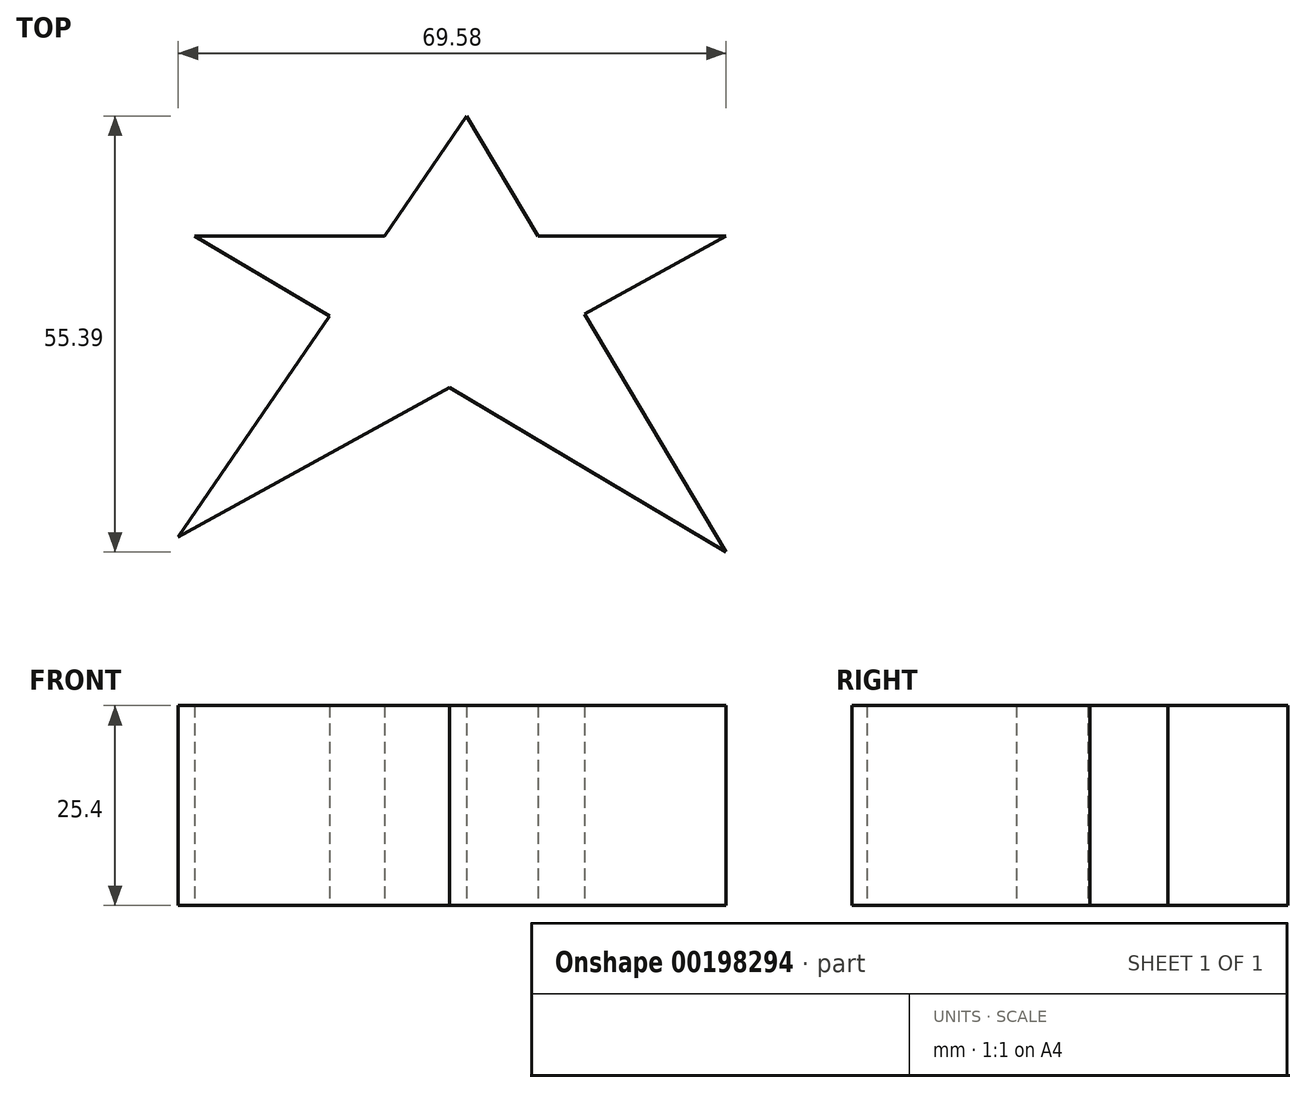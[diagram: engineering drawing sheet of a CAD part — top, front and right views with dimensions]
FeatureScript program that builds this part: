
annotation { "Feature Type Name" : "Feature", "Feature Type Description" : "" }
export const myFeature = defineFeature(function(context is Context, id is Id, definition is map)
    precondition{}
    {
        {
            var Q0;
            Q0=qCreatedBy(makeId("Top.planeOp"),FACE);
            var sketch = newSketch(context, id + "F0", { "sketchPlane" : qUnion([Q0])});
            skLineSegment(sketch, "E0", {"start": v(-42.06, -14.1) * mm, "end": v(-5.43, 39.35) * mm});
            skLineSegment(sketch, "E1", {"start": v(-5.43, 39.35) * mm, "end": v(27.52, -16.04) * mm});
            skLineSegment(sketch, "E2", {"start": v(27.52, -16.04) * mm, "end": v(-39.96, 24.1) * mm});
            skLineSegment(sketch, "E3", {"start": v(-39.96, 24.1) * mm, "end": v(27.52, 24.1) * mm});
            skLineSegment(sketch, "E4", {"start": v(27.52, 24.1) * mm, "end": v(-42.06, -14.1) * mm});
            skSolve(sketch);
        }
        {
            var Q0;
            {var subQ1=sQuery(id+"F0.wireOp",EDGE,"E0");var subQ5=sQuery(id+"F0.wireOp",EDGE,"E2");var subQ6=makeQuery(id+"F0.imprint","INTERSECT",VERTEX,{"derivedFrom":[subQ1,subQ5]});Q0=makeQuery(id+"F0.imprint","IMPRINT",FACE,{"disambiguationData":[TD([[makeQuery(id+"F0.imprint","IMPRINT",EDGE,{"disambiguationData":[TD([[subQ6,-1.0]])],"derivedFrom":subQ1}),-1.0]])]});}
            var Q1;
            {var subQ0=sQuery(id+"F0.wireOp",EDGE,"E2");var subQ1=sQuery(id+"F0.wireOp",EDGE,"E0");var subQ2=makeQuery(id+"F0.imprint","INTERSECT",VERTEX,{"derivedFrom":[subQ1,subQ0]});Q1=makeQuery(id+"F0.imprint","IMPRINT",FACE,{"disambiguationData":[TD([[makeQuery(id+"F0.imprint","IMPRINT",EDGE,{"disambiguationData":[TD([[subQ2,-1.0]])],"derivedFrom":subQ1}),1.0]])]});}
            var Q2;
            {var subQ0=sQuery(id+"F0.wireOp",EDGE,"E3");var subQ1=sQuery(id+"F0.wireOp",EDGE,"E1");var subQ2=makeQuery(id+"F0.imprint","INTERSECT",VERTEX,{"derivedFrom":[subQ1,subQ0]});Q2=makeQuery(id+"F0.imprint","IMPRINT",FACE,{"disambiguationData":[TD([[makeQuery(id+"F0.imprint","IMPRINT",EDGE,{"disambiguationData":[TD([[subQ2,-1.0]])],"derivedFrom":subQ1}),1.0]])]});}
            var Q3;
            {var subQ0=sQuery(id+"F0.wireOp",EDGE,"E1");var subQ1=sQuery(id+"F0.wireOp",EDGE,"E0");var subQ2=makeQuery(id+"F0.imprint","INTERSECT",VERTEX,{"derivedFrom":[subQ1,subQ0]});Q3=makeQuery(id+"F0.imprint","IMPRINT",FACE,{"disambiguationData":[TD([[makeQuery(id+"F0.imprint","IMPRINT",EDGE,{"disambiguationData":[TD([[subQ2,1.0]])],"derivedFrom":subQ1}),-1.0]])]});}
            var Q4;
            {var subQ0=sQuery(id+"F0.wireOp",EDGE,"E4");var subQ1=sQuery(id+"F0.wireOp",EDGE,"E0");var subQ2=makeQuery(id+"F0.imprint","INTERSECT",VERTEX,{"derivedFrom":[subQ1,subQ0]});Q4=makeQuery(id+"F0.imprint","IMPRINT",FACE,{"disambiguationData":[TD([[makeQuery(id+"F0.imprint","IMPRINT",EDGE,{"disambiguationData":[TD([[subQ2,-1.0]])],"derivedFrom":subQ1}),-1.0]])]});}
            var Q5;
            {var subQ0=sQuery(id+"F0.wireOp",EDGE,"E2");var subQ1=sQuery(id+"F0.wireOp",EDGE,"E1");var subQ2=makeQuery(id+"F0.imprint","INTERSECT",VERTEX,{"derivedFrom":[subQ1,subQ0]});Q5=makeQuery(id+"F0.imprint","IMPRINT",FACE,{"disambiguationData":[TD([[makeQuery(id+"F0.imprint","IMPRINT",EDGE,{"disambiguationData":[TD([[subQ2,1.0]])],"derivedFrom":subQ1}),-1.0]])]});}
            extrude(context, id + "F1", {"entities" : qUnion([Q0, Q1, Q2, Q3, Q4, Q5]), "depth" : 25.4 * mm});
        }
    });
